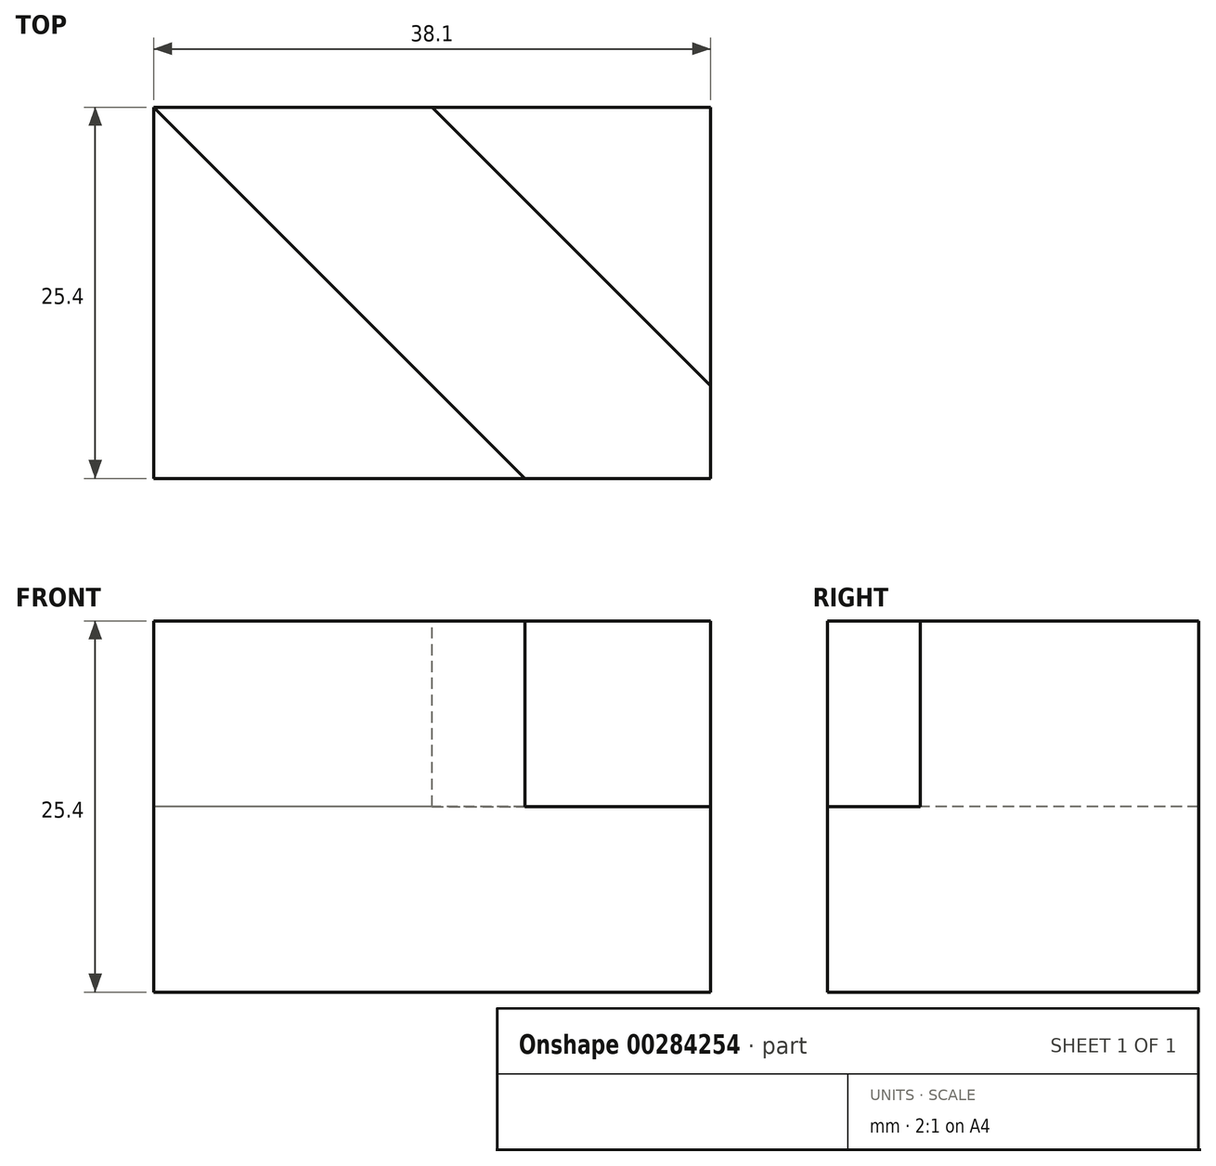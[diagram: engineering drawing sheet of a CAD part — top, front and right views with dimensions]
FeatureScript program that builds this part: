
annotation { "Feature Type Name" : "Feature", "Feature Type Description" : "" }
export const myFeature = defineFeature(function(context is Context, id is Id, definition is map)
    precondition{}
    {
        {
            var Q0;
            Q0=qCreatedBy(makeId("Front.planeOp"),FACE);
            var sketch = newSketch(context, id + "F0", { "sketchPlane" : qUnion([Q0])});
            skLineSegment(sketch, "E0", {"start": v(0, 0) * mm, "end": v(38.1, 0) * mm});
            skLineSegment(sketch, "E1", {"start": v(38.1, 0) * mm, "end": v(38.1, 25.4) * mm});
            skLineSegment(sketch, "E2", {"start": v(38.1, 25.4) * mm, "end": v(0, 25.4) * mm});
            skLineSegment(sketch, "E3", {"start": v(0, 25.4) * mm, "end": v(0, 0) * mm});
            skSolve(sketch);
        }
        {
            var Q0;
            Q0 = qSketchRegion(id + "F0", true);
            extrude(context, id + "F1", {"entities" : qUnion([Q0]), "depth" : 25.4 * mm});
        }
        {
            var Q0;
            Q0=makeQuery(id+"F1.opExtrude","SWEPT_FACE",FACE,{"disambiguationData":[OSD([sQuery(id+"F0.wireOp",EDGE,"E2")])]});
            var sketch = newSketch(context, id + "F2", { "sketchPlane" : qUnion([Q0])});
            skLineSegment(sketch, "E4", {"start": v(19.05, 0) * mm, "end": v(38.1, -19.05) * mm});
            skLineSegment(sketch, "E5", {"start": v(25.4, -25.4) * mm, "end": v(0, 0) * mm});
            skLineSegment(sketch, "E6", {"start": v(0, 0) * mm, "end": v(19.05, 0) * mm});
            skLineSegment(sketch, "E7", {"start": v(38.1, -19.05) * mm, "end": v(38.1, -25.4) * mm});
            skLineSegment(sketch, "E8", {"start": v(38.1, -25.4) * mm, "end": v(25.4, -25.4) * mm});
            skSolve(sketch);
        }
        {
            var Q0;
            Q0 = qSketchRegion(id + "F2", true);
            extrude(context, id + "F3", {"entities" : qUnion([Q0]), "operationType" : NewBodyOperationType.REMOVE, "oppositeDirection" : true, "depth" : 12.7 * mm});
        }
    });
